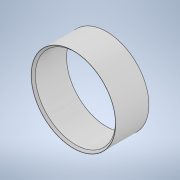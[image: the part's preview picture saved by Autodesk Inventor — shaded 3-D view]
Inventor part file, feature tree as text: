
AUTODESK INVENTOR PART (.ipt)
format: ipt  version: 2020.2 (Build 242310000, 310)  size: 251,904 bytes
history: native  units: mm
features: extrude x2, sketch x2, chamfer x1
ambient origin geometry x8: Origin, YZ Plane, XZ Plane, XY Plane, X Axis, Y Axis, Z Axis, Center Point
bodies: Solid1 (feature_tree)
feature tree (5):
  extrude  "Extrusion1"  Depth=1.0mm TaperAngle=45.0deg
  chamfer  "Chamfer1"  Distance=1.5mm
  extrude  "Extrusion2"  Depth=41.55mm
  sketch  "Sketch1"  dims[d1=17.8mm d2=0.0mm d3=1.0mm d4=2.0mm d5=45.0deg d6=1.5mm d7=0.0mm]
  sketch  "Sketch2"  dims[d9=1.096917mm d10=41.55mm]
